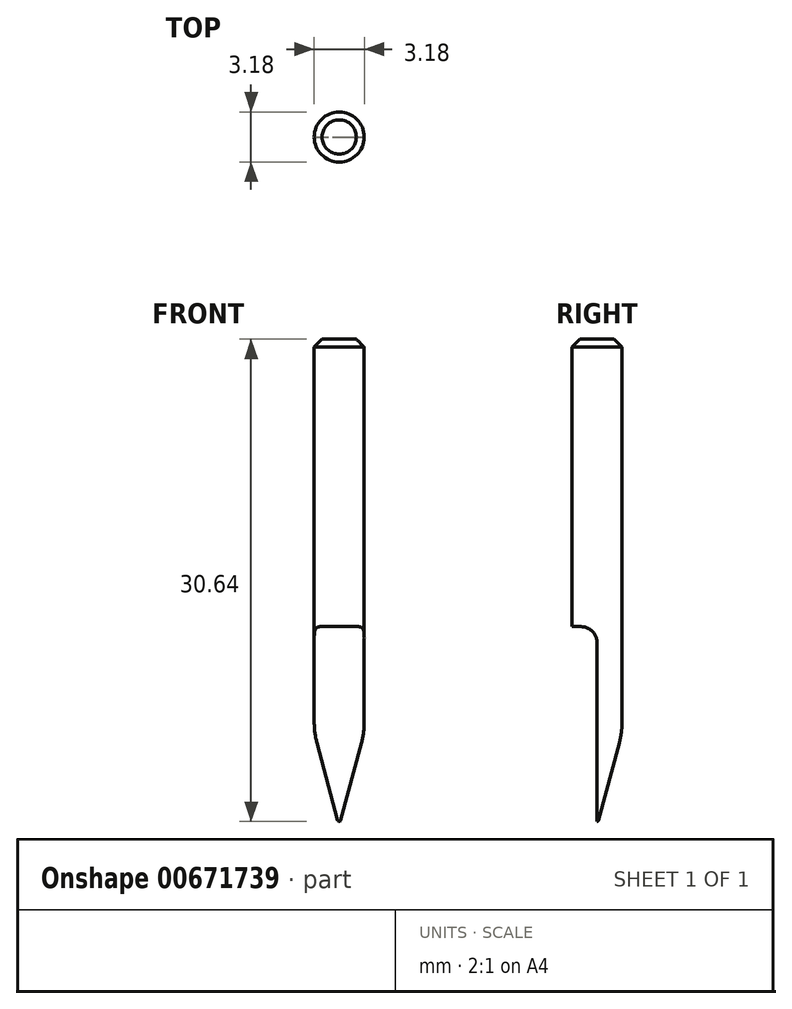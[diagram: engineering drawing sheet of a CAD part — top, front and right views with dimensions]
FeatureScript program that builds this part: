
annotation { "Feature Type Name" : "Feature", "Feature Type Description" : "" }
export const myFeature = defineFeature(function(context is Context, id is Id, definition is map)
    precondition{}
    {
        {
            var Q0;
            Q0=qCreatedBy(makeId("Top.planeOp"),FACE);
            var sketch = newSketch(context, id + "F0", { "sketchPlane" : qUnion([Q0])});
            skCircle(sketch, "E0", {"center": v(0, 0) * mm, "radius": 1.59 * mm});
            skSolve(sketch);
        }
        {
            var Q0;
            Q0=qSketchRegion(id+"F0",true);
            extrude(context, id + "F1", {"entities" : qUnion([Q0]), "depth" : 25 * mm, "offsetDistance" : 25 * mm});
        }
        {
            var Q0;
            Q0=qCreatedBy(makeId("Front.planeOp"),FACE);
            var sketch = newSketch(context, id + "F2", { "sketchPlane" : qUnion([Q0])});
            skLineSegment(sketch, "E1", {"start": v(0, 0) * mm, "end": v(-1.59, 0) * mm});
            skLineSegment(sketch, "E2", {"start": v(-1.59, 0) * mm, "end": v(-0.1, -5.56) * mm});
            skLineSegment(sketch, "E3", {"start": v(0, -5.64) * mm, "end": v(0, 0) * mm});
            skArc(sketch, "E4", {"start": v(-0.1, -5.56) * mm, "mid": v(-0.06, -5.62) * mm, "end": v(0, -5.64) * mm});
            skSolve(sketch);
        }
        {
            var Q0;
            Q0=qSketchRegion(id+"F2",true);
            var Q1;
            Q1=sQuery(id+"F2.wireOp",EDGE,"E3");
            revolve(context, id + "F3", {"operationType" : NewBodyOperationType.ADD, "entities" : qUnion([Q0]), "axis" : qUnion([Q1]), "revolveType" : RevolveType.FULL});
        }
        {
            var Q0;
            Q0=makeQuery(id+"F3.opRevolve","SWEPT_FACE",FACE,{"disambiguationData":[OSD([sQuery(id+"F2.wireOp",EDGE,"E2")])]});
            fillet(context, id + "F4", {"entities" : qUnion([Q0]), "radius" : 5 * mm, "tangentPropagation" : true, "allowEdgeOverflow" : false});
        }
        {
            var Q0;
            Q0=qCreatedBy(makeId("Right.planeOp"),FACE);
            var sketch = newSketch(context, id + "F5", { "sketchPlane" : qUnion([Q0])});
            skLineSegment(sketch, "E5.bottom", {"start": v(-1, 6.74) * mm, "end": v(-3.29, 6.74) * mm});
            skLineSegment(sketch, "E5.top", {"start": v(0, -6.52) * mm, "end": v(-3.29, -6.52) * mm});
            skLineSegment(sketch, "E5.left", {"start": v(0, 5.74) * mm, "end": v(0, -6.52) * mm});
            skLineSegment(sketch, "E5.right", {"start": v(-3.29, 6.74) * mm, "end": v(-3.29, -6.52) * mm});
            skPoint(sketch, "E6.visualSharp", {"position": v(0, 6.74) * mm});
            skArc(sketch, "E6.filletArc", {"start": v(0, 5.74) * mm, "mid": v(-0.3, 6.45) * mm, "end": v(-1, 6.74) * mm});
            skSolve(sketch);
        }
        {
            var Q0;
            Q0=qSketchRegion(id+"F5",true);
            extrude(context, id + "F6", {"entities" : qUnion([Q0]), "operationType" : NewBodyOperationType.REMOVE, "oppositeDirection" : true, "depth" : 25 * mm, "offsetDistance" : 25 * mm, "symmetric" : true});
        }
        {
            var Q0;
            Q0=makeQuery(id+"F1.opExtrude","CAP_EDGE",EDGE,{"disambiguationData":[OSD([sQuery(id+"F0.wireOp",EDGE,"E0")])],"isStart":false});
            chamfer(context, id + "F7", {"entities" : qUnion([Q0]), "width" : 0.5 * mm, "tangentPropagation" : true});
        }
    });
